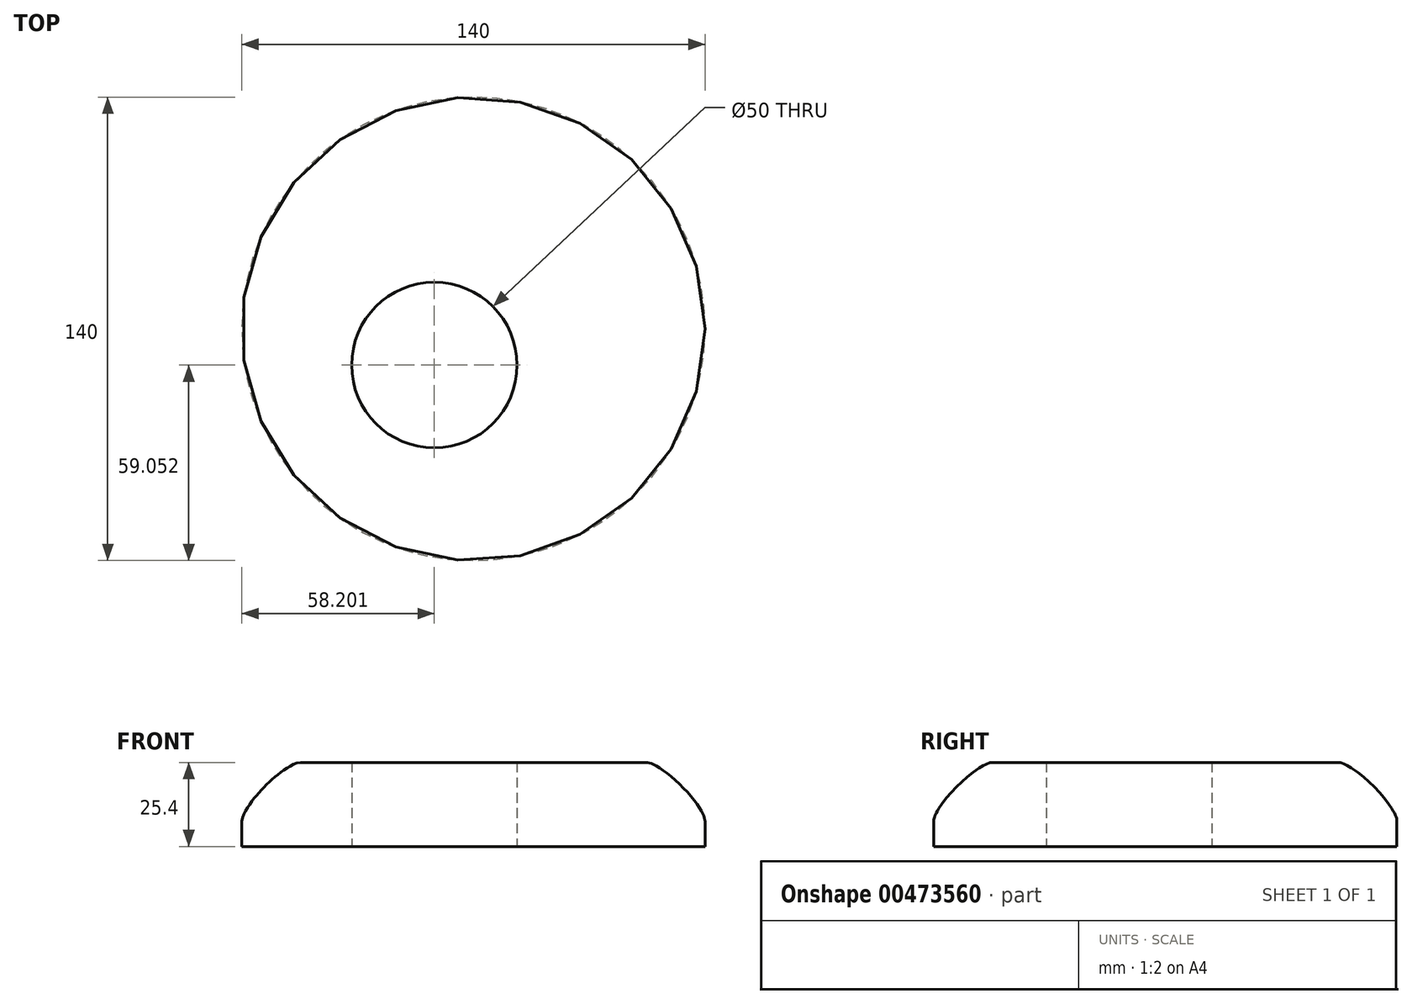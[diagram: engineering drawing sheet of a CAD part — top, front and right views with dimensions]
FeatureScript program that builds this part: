
annotation { "Feature Type Name" : "Feature", "Feature Type Description" : "" }
export const myFeature = defineFeature(function(context is Context, id is Id, definition is map)
    precondition{}
    {
        {
            var Q0;
            Q0=qCreatedBy(makeId("Top.planeOp"),FACE);
            var sketch = newSketch(context, id + "F0", { "sketchPlane" : qUnion([Q0])});
            skCircle(sketch, "E0", {"center": v(-48.47, -10.95) * mm, "radius": 25 * mm});
            skCircle(sketch, "E1", {"center": v(-36.67, 0) * mm, "radius": 70 * mm});
            skSolve(sketch);
        }
        {
            var Q0;
            Q0 = qSketchRegion(id + "F0", true);
            extrude(context, id + "F1", {"entities" : qUnion([Q0]), "depth" : 25.4 * mm});
        }
        {
            var Q0;
            Q0=makeQuery(id+"F1.opExtrude","CAP_EDGE",EDGE,{"disambiguationData":[OSD([sQuery(id+"F0.wireOp",EDGE,"E1")])],"isStart":false});
            fillet(context, id + "F2", {"entities" : qUnion([Q0]), "radius" : 17.78 * mm, "tangentPropagation" : true, "rho" : 0.2, "crossSection" : FilletCrossSection.CONIC, "allowEdgeOverflow" : false});
        }
    });
